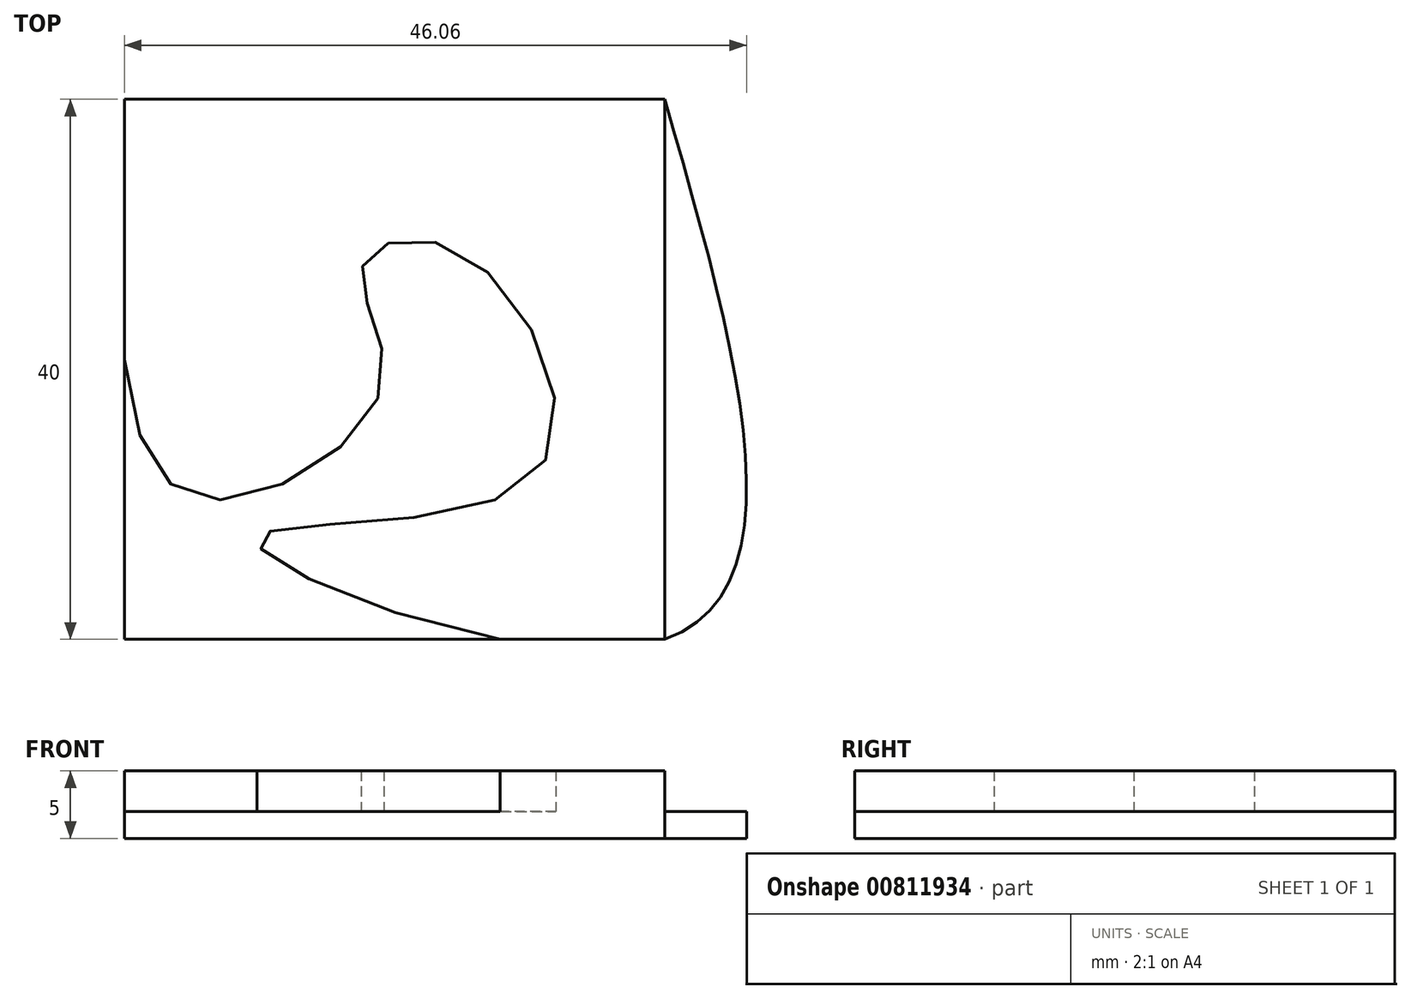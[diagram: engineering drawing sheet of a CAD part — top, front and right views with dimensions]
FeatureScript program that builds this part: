
annotation { "Feature Type Name" : "Feature", "Feature Type Description" : "" }
export const myFeature = defineFeature(function(context is Context, id is Id, definition is map)
    precondition{}
    {
        {
            var Q0;
            Q0=qCreatedBy(makeId("Top.planeOp"),FACE);
            var sketch = newSketch(context, id + "F0", { "sketchPlane" : qUnion([Q0])});
            skLineSegment(sketch, "E0.bottom", {"start": v(-47.5, 50.3) * mm, "end": v(-7.5, 50.3) * mm});
            skLineSegment(sketch, "E0.top", {"start": v(-47.5, 10.3) * mm, "end": v(-7.5, 10.3) * mm});
            skLineSegment(sketch, "E0.left", {"start": v(-47.5, 50.3) * mm, "end": v(-47.5, 10.3) * mm});
            skLineSegment(sketch, "E0.right", {"start": v(-7.5, 50.3) * mm, "end": v(-7.5, 10.3) * mm});
            skFitSpline(sketch, "E1", {"points": [v(-47.5, 50.3) * mm, v(-42.47, 20.89) * mm, v(-28.48, 28.88) * mm, v(-29.88, 37.88) * mm, v(-22.49, 38.88) * mm, v(-17.29, 22.29) * mm, v(-37.68, 17.69) * mm, v(-7.5, 10.3) * mm, v(-7.5, 50.3) * mm], "startDerivative": vector(-11.4, -269.86) * mm, "endDerivative": vector(-89.23, 309.63) * mm});
            skLineSegment(sketch, "E2.bottom", {"start": v(12.42, 53.51) * mm, "end": v(52.42, 53.51) * mm});
            skLineSegment(sketch, "E2.top", {"start": v(12.42, 13.51) * mm, "end": v(52.42, 13.51) * mm});
            skLineSegment(sketch, "E2.left", {"start": v(12.42, 53.51) * mm, "end": v(12.42, 13.51) * mm});
            skLineSegment(sketch, "E2.right", {"start": v(52.42, 53.51) * mm, "end": v(52.42, 13.51) * mm});
            skFitSpline(sketch, "E3", {"points": [v(12.42, 53.51) * mm, v(17.44, 24.1) * mm, v(31.43, 32.1) * mm, v(30.03, 41.1) * mm, v(37.43, 42.1) * mm, v(42.62, 25.5) * mm, v(22.24, 20.9) * mm, v(52.42, 13.51) * mm, v(52.42, 53.51) * mm], "startDerivative": vector(-11.4, -269.86) * mm, "endDerivative": vector(-89.23, 309.63) * mm});
            skSolve(sketch);
        }
        {
            var Q0;
            {var subQ2=sQuery(id+"F0.wireOp",EDGE,"E0.bottom");Q0=makeQuery(id+"F0.imprint","IMPRINT",FACE,{"disambiguationData":[TD([[makeQuery(id+"F0.imprint","IMPRINT",EDGE,{"derivedFrom":subQ2}),-1.0]])]});}
            extrude(context, id + "F1", {"entities" : qUnion([Q0]), "depth" : 5 * mm, "offsetDistance" : 25 * mm});
        }
        {
            var Q0;
            {var subQ0=sQuery(id+"F0.wireOp",EDGE,"E0.left");var subQ1=sQuery(id+"F0.wireOp",EDGE,"E0.top");var subQ2=makeQuery(id+"F0.imprint","INTERSECT",VERTEX,{"derivedFrom":[subQ1,subQ0]});Q0=makeQuery(id+"F0.imprint","IMPRINT",FACE,{"disambiguationData":[TD([[makeQuery(id+"F0.imprint","IMPRINT",EDGE,{"disambiguationData":[TD([[subQ2,-1.0]])],"derivedFrom":subQ1}),1.0]])]});}
            var Q1;
            {var subQ0=sQuery(id+"F0.wireOp",EDGE,"E0.right");Q1=makeQuery(id+"F0.imprint","IMPRINT",FACE,{"disambiguationData":[TD([[makeQuery(id+"F0.imprint","IMPRINT",EDGE,{"derivedFrom":subQ0}),1.0]])]});}
            extrude(context, id + "F2", {"entities" : qUnion([Q0, Q1]), "operationType" : NewBodyOperationType.ADD, "depth" : 2 * mm, "offsetDistance" : 25 * mm});
        }
    });
